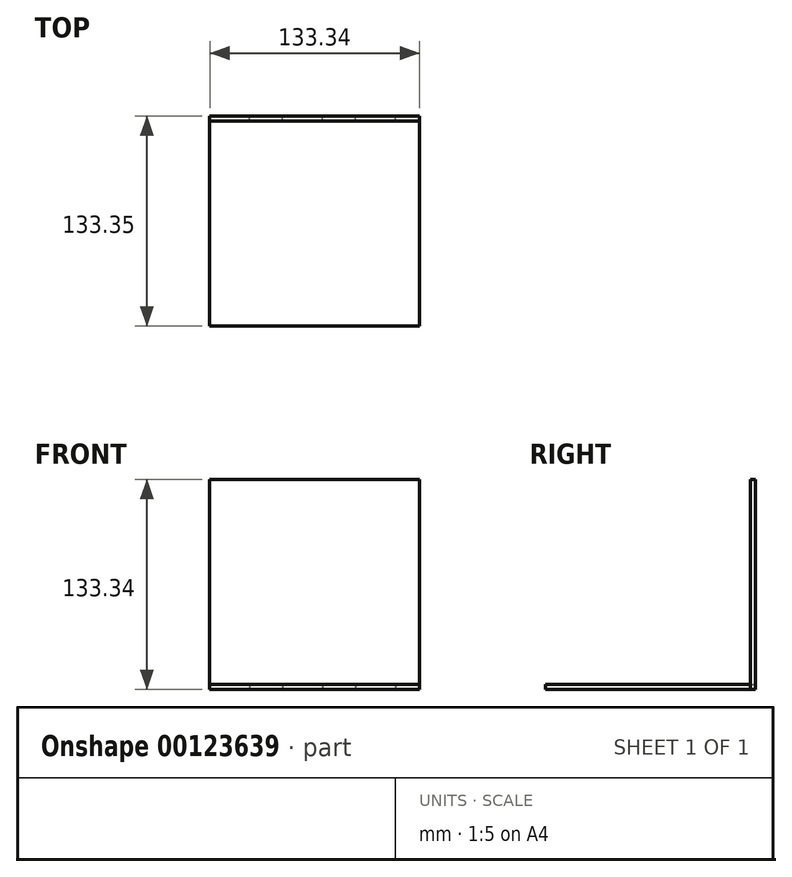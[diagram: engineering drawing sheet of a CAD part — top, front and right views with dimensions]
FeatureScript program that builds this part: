
annotation { "Feature Type Name" : "Feature", "Feature Type Description" : "" }
export const myFeature = defineFeature(function(context is Context, id is Id, definition is map)
    precondition{}
    {
        {
            var Q0;
            Q0=qCreatedBy(makeId("Front.planeOp"),FACE);
            var sketch = newSketch(context, id + "F0", { "sketchPlane" : qUnion([Q0])});
            skLineSegment(sketch, "E0.bottom", {"start": v(66.68, -66.67) * mm, "end": v(-66.68, -66.68) * mm});
            skLineSegment(sketch, "E0.top", {"start": v(66.68, 66.68) * mm, "end": v(-66.68, 66.67) * mm});
            skLineSegment(sketch, "E0.left", {"start": v(66.68, -66.68) * mm, "end": v(66.68, 66.68) * mm});
            skLineSegment(sketch, "E0.right", {"start": v(-66.68, -66.68) * mm, "end": v(-66.68, 66.68) * mm});
            skPoint(sketch, "E0.middle", {"position": v(0, 0) * mm});
            skSolve(sketch);
        }
        {
            var Q0;
            Q0 = qSketchRegion(id + "F0", true);
            extrude(context, id + "F1", {"entities" : qUnion([Q0]), "depth" : 3.17 * mm});
        }
        {
            var Q0;
            Q0=makeQuery(id+"F0.imprint","IMPRINT",FACE,{"disambiguationData":[TD([[makeQuery(id+"F0.imprint","IMPRINT",EDGE,{"derivedFrom":sQuery(id+"F0.wireOp",EDGE,"E0.bottom")}),-1.0]])]});
            var sketch = newSketch(context, id + "F2", { "sketchPlane" : qUnion([Q0])});
            skLineSegment(sketch, "E1.bottom", {"start": v(-66.68, -66.68) * mm, "end": v(66.68, -66.68) * mm});
            skLineSegment(sketch, "E1.top", {"start": v(-66.68, -63.5) * mm, "end": v(66.68, -63.5) * mm});
            skLineSegment(sketch, "E1.left", {"start": v(-66.68, -66.68) * mm, "end": v(-66.68, -63.5) * mm});
            skLineSegment(sketch, "E1.right", {"start": v(66.68, -66.68) * mm, "end": v(66.68, -63.5) * mm});
            skSolve(sketch);
        }
        {
            var Q0;
            Q0=makeQuery(id+"F2.imprint","IMPRINT",FACE,{"disambiguationData":[TD([[makeQuery(id+"F2.imprint","IMPRINT",EDGE,{"derivedFrom":sQuery(id+"F2.wireOp",EDGE,"E1.bottom")}),-1.0]])]});
            extrude(context, id + "F3", {"entities" : qUnion([Q0]), "depth" : 133.35 * mm});
        }
        {
            var Q0;
            Q0=makeQuery(id+"F1.opExtrude","SWEPT_FACE",FACE,{"disambiguationData":[OSD([sQuery(id+"F0.wireOp",EDGE,"E0.bottom")])]});
            var sketch = newSketch(context, id + "F4", { "sketchPlane" : qUnion([Q0])});
            skLineSegment(sketch, "E2.bottom", {"start": v(-66.68, 3.18) * mm, "end": v(-41.28, 3.18) * mm});
            skLineSegment(sketch, "E2.top", {"start": v(-66.68, 0) * mm, "end": v(-41.28, 0) * mm});
            skLineSegment(sketch, "E2.left", {"start": v(-66.68, 3.18) * mm, "end": v(-66.68, 0) * mm});
            skLineSegment(sketch, "E2.right", {"start": v(-41.28, 3.18) * mm, "end": v(-41.28, 0) * mm});
            skLineSegment(sketch, "E3.bottom", {"start": v(-20.32, 3.18) * mm, "end": v(5.08, 3.18) * mm});
            skLineSegment(sketch, "E3.top", {"start": v(-20.32, 0) * mm, "end": v(5.08, 0) * mm});
            skLineSegment(sketch, "E3.left", {"start": v(-20.32, 3.18) * mm, "end": v(-20.32, 0) * mm});
            skLineSegment(sketch, "E3.right", {"start": v(5.08, 3.18) * mm, "end": v(5.08, 0) * mm});
            skLineSegment(sketch, "E4.bottom", {"start": v(26.03, 3.18) * mm, "end": v(51.43, 3.18) * mm});
            skLineSegment(sketch, "E4.top", {"start": v(26.03, 0) * mm, "end": v(51.43, 0) * mm});
            skLineSegment(sketch, "E4.left", {"start": v(26.03, 3.18) * mm, "end": v(26.03, 0) * mm});
            skLineSegment(sketch, "E4.right", {"start": v(51.43, 3.18) * mm, "end": v(51.43, 0) * mm});
            skSolve(sketch);
        }
        {
            var Q0;
            Q0 = qSketchRegion(id + "F4", true);
            extrude(context, id + "F5", {"entities" : qUnion([Q0]), "operationType" : NewBodyOperationType.REMOVE, "oppositeDirection" : true, "depth" : 3.17 * mm});
        }
        {
            var Q0;
            Q0=makeQuery(id+"F1.opExtrude","SWEPT_BODY",BODY,{"disambiguationData":[OSD([sQuery(id+"F0.wireOp",EDGE,"E0.bottom"),sQuery(id+"F0.wireOp",EDGE,"E0.top"),sQuery(id+"F0.wireOp",EDGE,"E0.left"),sQuery(id+"F0.wireOp",EDGE,"E0.right")])]});
            var Q1;
            Q1=makeQuery(id+"F3.opExtrude","SWEPT_BODY",BODY,{"disambiguationData":[OSD([sQuery(id+"F2.wireOp",EDGE,"E1.bottom"),sQuery(id+"F2.wireOp",EDGE,"E1.top"),sQuery(id+"F2.wireOp",EDGE,"E1.left"),sQuery(id+"F2.wireOp",EDGE,"E1.right")])]});
            booleanBodies(context, id + "F6", {"operationType" : BooleanOperationType.SUBTRACTION, "tools" : qUnion([Q0]), "targets" : qUnion([Q1]), "keepTools" : true});
        }
    });
